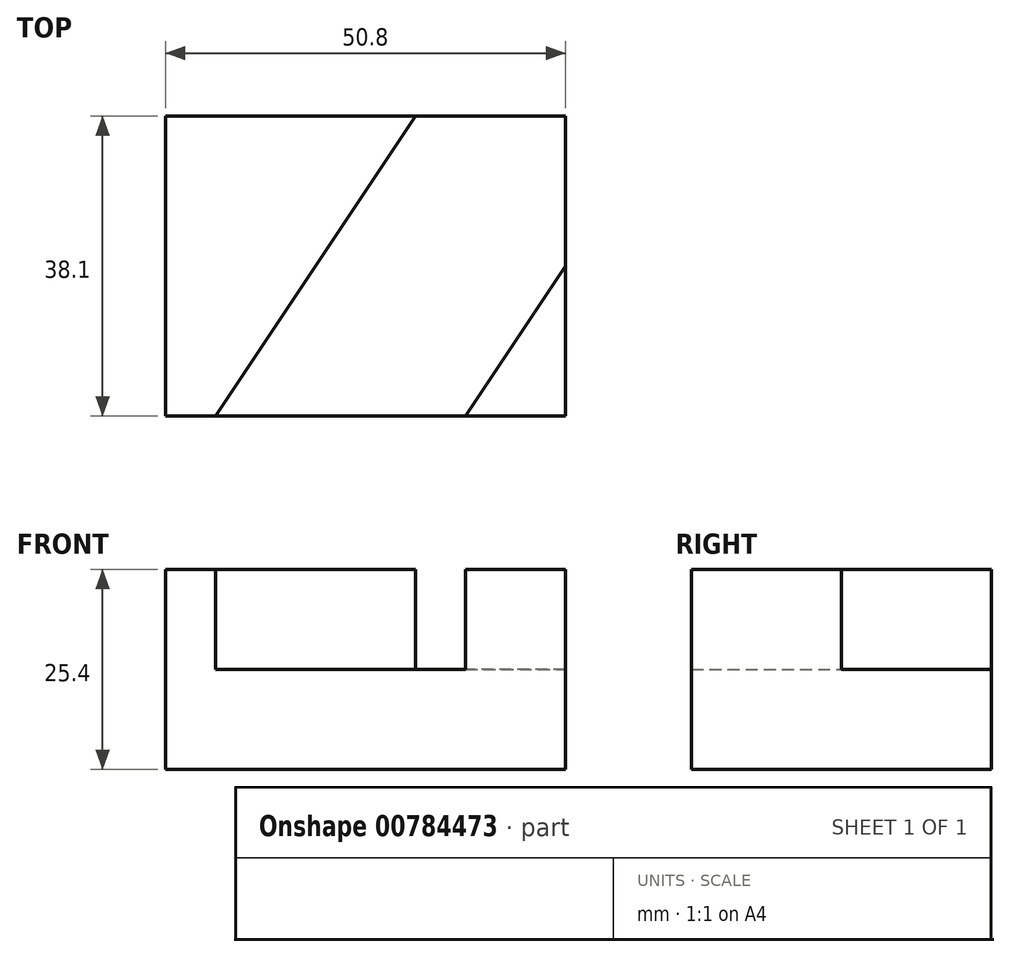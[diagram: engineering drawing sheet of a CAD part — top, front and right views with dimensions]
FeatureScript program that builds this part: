
annotation { "Feature Type Name" : "Feature", "Feature Type Description" : "" }
export const myFeature = defineFeature(function(context is Context, id is Id, definition is map)
    precondition{}
    {
        {
            var Q0;
            Q0=qCreatedBy(makeId("Front.planeOp"),FACE);
            var sketch = newSketch(context, id + "F0", { "sketchPlane" : qUnion([Q0])});
            skLineSegment(sketch, "E0", {"start": v(0, 0) * mm, "end": v(50.8, 0) * mm});
            skLineSegment(sketch, "E1", {"start": v(50.8, 0) * mm, "end": v(50.8, 25.4) * mm});
            skLineSegment(sketch, "E2", {"start": v(50.8, 25.4) * mm, "end": v(0, 25.4) * mm});
            skLineSegment(sketch, "E3", {"start": v(0, 25.4) * mm, "end": v(0, 0) * mm});
            skSolve(sketch);
        }
        {
            var Q0;
            Q0 = qSketchRegion(id + "F0", true);
            extrude(context, id + "F1", {"entities" : qUnion([Q0]), "depth" : 38.1 * mm, "offsetDistance" : 25.4 * mm});
        }
        {
            var Q0;
            Q0=makeQuery(id+"F1.opExtrude","SWEPT_FACE",FACE,{"disambiguationData":[OSD([sQuery(id+"F0.wireOp",EDGE,"E2")])]});
            var sketch = newSketch(context, id + "F2", { "sketchPlane" : qUnion([Q0])});
            skLineSegment(sketch, "E4", {"start": v(50.8, 0) * mm, "end": v(31.75, 0) * mm});
            skLineSegment(sketch, "E5", {"start": v(50.8, 0) * mm, "end": v(50.8, -19.05) * mm});
            skLineSegment(sketch, "E6", {"start": v(0, -38.1) * mm, "end": v(6.35, -38.1) * mm});
            skLineSegment(sketch, "E7", {"start": v(6.35, -38.1) * mm, "end": v(31.75, 0) * mm});
            skLineSegment(sketch, "E8", {"start": v(6.35, -38.1) * mm, "end": v(38.1, -38.1) * mm});
            skLineSegment(sketch, "E9", {"start": v(38.1, -38.1) * mm, "end": v(50.8, -19.05) * mm});
            skSolve(sketch);
        }
        {
            var Q0;
            Q0=makeQuery(id+"F2.imprint","IMPRINT",FACE,{"disambiguationData":[TD([[makeQuery(id+"F2.imprint","IMPRINT",EDGE,{"derivedFrom":sQuery(id+"F2.wireOp",EDGE,"E4")}),1.0]])]});
            extrude(context, id + "F3", {"entities" : qUnion([Q0]), "operationType" : NewBodyOperationType.REMOVE, "oppositeDirection" : true, "depth" : 12.7 * mm, "offsetDistance" : 25.4 * mm});
        }
    });
